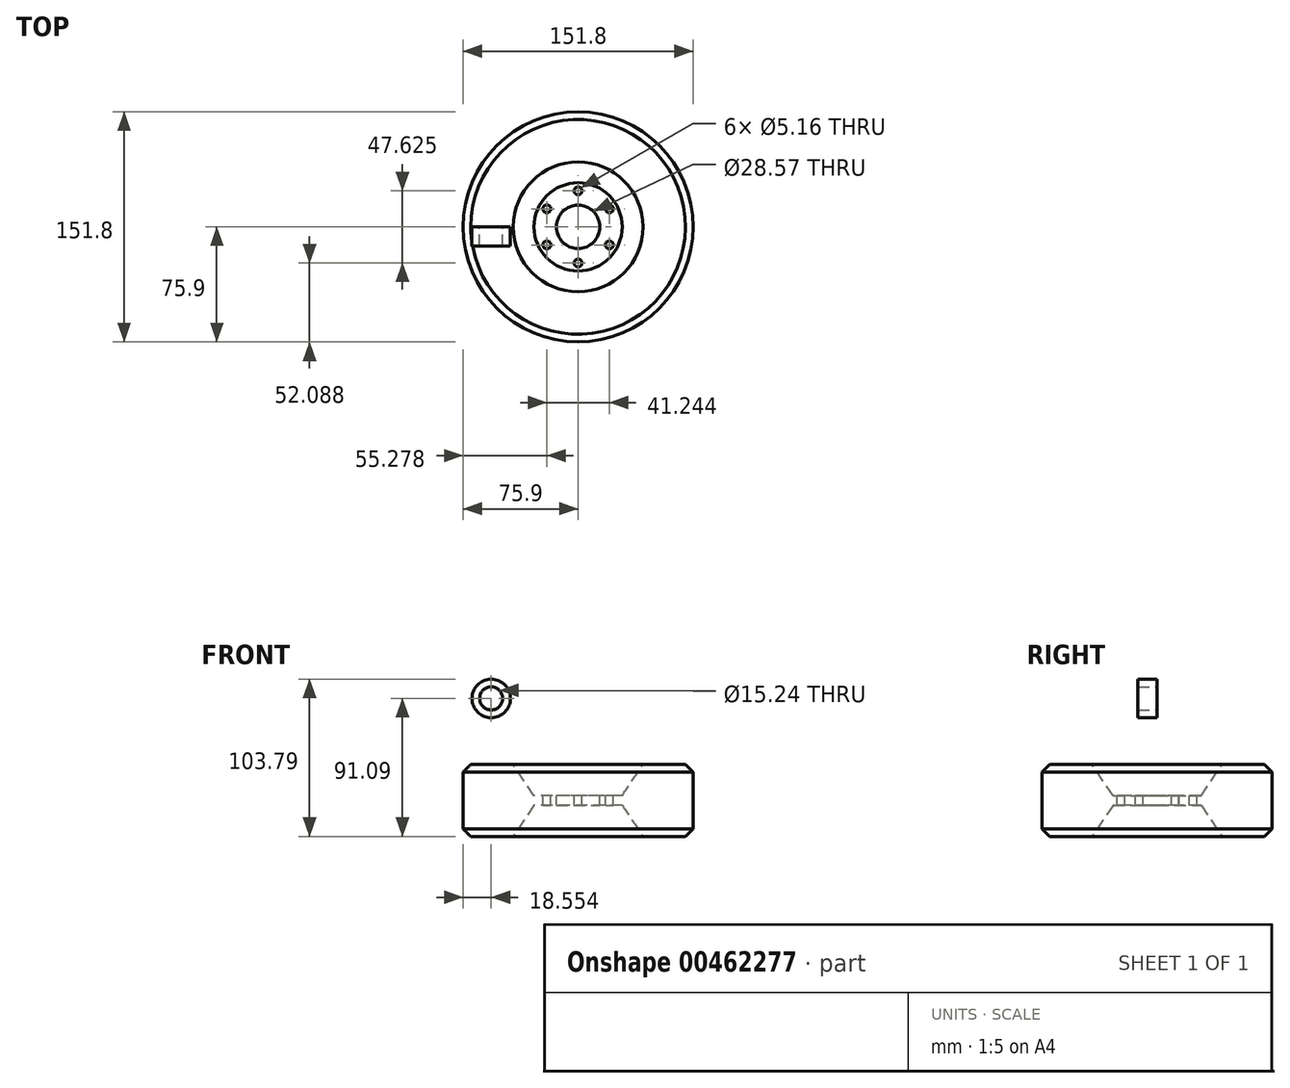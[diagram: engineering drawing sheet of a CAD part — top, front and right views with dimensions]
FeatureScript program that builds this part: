
annotation { "Feature Type Name" : "Feature", "Feature Type Description" : "" }
export const myFeature = defineFeature(function(context is Context, id is Id, definition is map)
    precondition{}
    {
        {
            var Q0;
            Q0=qCreatedBy(makeId("Front.planeOp"),FACE);
            var sketch = newSketch(context, id + "F0", { "sketchPlane" : qUnion([Q0])});
            skLineSegment(sketch, "E0.bottom", {"start": v(-75.9, 23.79) * mm, "end": v(-42.86, 23.79) * mm});
            skLineSegment(sketch, "E0.top", {"start": v(-75.9, -23.79) * mm, "end": v(-42.86, -23.79) * mm});
            skLineSegment(sketch, "E0.left", {"start": v(-75.9, 23.79) * mm, "end": v(-75.9, -23.79) * mm});
            skLineSegment(sketch, "E0.right", {"start": v(75.9, 23.79) * mm, "end": v(75.9, -23.79) * mm, "construction": true});
            skPoint(sketch, "E0.middle", {"position": v(0, 0) * mm});
            skLineSegment(sketch, "E1.bottom", {"start": v(-42.86, 23.79) * mm, "end": v(42.86, 23.79) * mm, "construction": true});
            skLineSegment(sketch, "E1.top", {"start": v(-42.86, -23.79) * mm, "end": v(42.86, -23.79) * mm, "construction": true});
            skLineSegment(sketch, "E1.left", {"start": v(-42.86, 23.79) * mm, "end": v(-42.86, -23.79) * mm, "construction": true});
            skLineSegment(sketch, "E1.right", {"start": v(42.86, 23.79) * mm, "end": v(42.86, -23.79) * mm, "construction": true});
            skLineSegment(sketch, "E2.bottom", {"start": v(-29.1, 3.18) * mm, "end": v(0, 3.18) * mm});
            skLineSegment(sketch, "E2.top", {"start": v(-29.1, -3.18) * mm, "end": v(0, -3.18) * mm});
            skLineSegment(sketch, "E2.left", {"start": v(-29.1, 3.18) * mm, "end": v(-29.1, -3.17) * mm, "construction": true});
            skLineSegment(sketch, "E2.right", {"start": v(29.1, 3.18) * mm, "end": v(29.1, -3.18) * mm, "construction": true});
            skLineSegment(sketch, "E3", {"start": v(-42.86, 23.79) * mm, "end": v(75.9, 23.79) * mm, "construction": true});
            skLineSegment(sketch, "E4", {"start": v(-42.86, -23.79) * mm, "end": v(75.9, -23.79) * mm, "construction": true});
            skLineSegment(sketch, "E5", {"start": v(-42.86, 23.79) * mm, "end": v(-29.1, 3.18) * mm});
            skLineSegment(sketch, "E6", {"start": v(-42.86, -23.79) * mm, "end": v(-29.1, -3.18) * mm});
            skLineSegment(sketch, "E7", {"start": v(0, 23.79) * mm, "end": v(0, -23.79) * mm});
            skLineSegment(sketch, "E8", {"start": v(0, 3.18) * mm, "end": v(29.1, 3.18) * mm, "construction": true});
            skLineSegment(sketch, "E9", {"start": v(0, -3.18) * mm, "end": v(29.1, -3.18) * mm, "construction": true});
            skSolve(sketch);
        }
        {
            var Q0;
            Q0=makeQuery(id+"F0.imprint","IMPRINT",FACE,{"disambiguationData":[TD([[makeQuery(id+"F0.imprint","IMPRINT",EDGE,{"derivedFrom":sQuery(id+"F0.wireOp",EDGE,"E0.bottom")}),-1.0]])]});
            var Q1;
            Q1=sQuery(id+"F0.wireOp",EDGE,"E7");
            revolve(context, id + "F1", {"entities" : qUnion([Q0]), "axis" : qUnion([Q1]), "revolveType" : RevolveType.FULL});
        }
        {
            var Q0;
            Q0=makeQuery(id+"F1.opRevolve","SWEPT_FACE",FACE,{"disambiguationData":[OSD([sQuery(id+"F0.wireOp",EDGE,"E2.bottom")])]});
            var sketch = newSketch(context, id + "F2", { "sketchPlane" : qUnion([Q0])});
            skCircle(sketch, "E10", {"center": v(0, 0) * mm, "radius": 23.81 * mm, "construction": true});
            skCircle(sketch, "E11", {"center": v(0, 0) * mm, "radius": 14.29 * mm});
            skCircle(sketch, "E12", {"center": v(0, 23.81) * mm, "radius": 2.58 * mm});
            skCircle(sketch, "E13.1.1", {"center": v(-20.62, 11.9) * mm, "radius": 2.58 * mm});
            skCircle(sketch, "E13.2.1", {"center": v(-20.62, -11.9) * mm, "radius": 2.58 * mm});
            skCircle(sketch, "E14.2.3.0", {"center": v(0, -23.81) * mm, "radius": 2.58 * mm});
            skCircle(sketch, "E14.2.4.0", {"center": v(20.62, -11.9) * mm, "radius": 2.58 * mm});
            skCircle(sketch, "E14.2.5.0", {"center": v(20.62, 11.9) * mm, "radius": 2.58 * mm});
            skLineSegment(sketch, "E15", {"start": v(0, 23.81) * mm, "end": v(0, 0) * mm, "construction": true});
            skSolve(sketch);
        }
        {
            var Q0;
            Q0=makeQuery(id+"F2.imprint","IMPRINT",FACE,{"disambiguationData":[TD([[makeQuery(id+"F2.imprint","IMPRINT",EDGE,{"derivedFrom":sQuery(id+"F2.wireOp",EDGE,"E13.1.1")}),1.0]])]});
            var Q1;
            Q1=makeQuery(id+"F2.imprint","IMPRINT",FACE,{"disambiguationData":[TD([[makeQuery(id+"F2.imprint","IMPRINT",EDGE,{"derivedFrom":sQuery(id+"F2.wireOp",EDGE,"E13.2.1")}),1.0]])]});
            var Q2;
            Q2=makeQuery(id+"F2.imprint","IMPRINT",FACE,{"disambiguationData":[TD([[makeQuery(id+"F2.imprint","IMPRINT",EDGE,{"derivedFrom":sQuery(id+"F2.wireOp",EDGE,"E11")}),1.0]])]});
            var Q3;
            Q3=makeQuery(id+"F2.imprint","IMPRINT",FACE,{"disambiguationData":[TD([[makeQuery(id+"F2.imprint","IMPRINT",EDGE,{"derivedFrom":sQuery(id+"F2.wireOp",EDGE,"E14.2.5.0")}),1.0]])]});
            var Q4;
            Q4=makeQuery(id+"F2.imprint","IMPRINT",FACE,{"disambiguationData":[TD([[makeQuery(id+"F2.imprint","IMPRINT",EDGE,{"derivedFrom":sQuery(id+"F2.wireOp",EDGE,"E12")}),1.0]])]});
            var Q5;
            Q5=makeQuery(id+"F2.imprint","IMPRINT",FACE,{"disambiguationData":[TD([[makeQuery(id+"F2.imprint","IMPRINT",EDGE,{"derivedFrom":sQuery(id+"F2.wireOp",EDGE,"E14.2.3.0")}),1.0]])]});
            var Q6;
            Q6=makeQuery(id+"F2.imprint","IMPRINT",FACE,{"disambiguationData":[TD([[makeQuery(id+"F2.imprint","IMPRINT",EDGE,{"derivedFrom":sQuery(id+"F2.wireOp",EDGE,"E14.2.4.0")}),1.0]])]});
            extrude(context, id + "F3", {"entities" : qUnion([Q0, Q1, Q2, Q3, Q4, Q5, Q6]), "operationType" : NewBodyOperationType.REMOVE, "endBound" : BoundingType.THROUGH_ALL, "oppositeDirection" : true, "depth" : 25.4 * mm});
        }
        {
            var Q0;
            Q0=makeQuery(id+"F1.opRevolve","SWEPT_EDGE",EDGE,{"disambiguationData":[OSD([sQuery(id+"F0.wireOp",EDGE,"E0.bottom"),sQuery(id+"F0.wireOp",EDGE,"E0.left")])]});
            var Q1;
            Q1=makeQuery(id+"F1.opRevolve","SWEPT_EDGE",EDGE,{"disambiguationData":[OSD([sQuery(id+"F0.wireOp",EDGE,"E0.top"),sQuery(id+"F0.wireOp",EDGE,"E0.left")])]});
            chamfer(context, id + "F4", {"entities" : qUnion([Q0, Q1]), "width" : 5.08 * mm, "tangentPropagation" : true});
        }
        {
            var Q0;
            Q0=qCreatedBy(makeId("Front.planeOp"),FACE);
            var sketch = newSketch(context, id + "F5", { "sketchPlane" : qUnion([Q0])});
            skCircle(sketch, "E16", {"center": v(-57.35, 67.3) * mm, "radius": 12.7 * mm});
            skCircle(sketch, "E17", {"center": v(-57.35, 67.3) * mm, "radius": 7.62 * mm});
            skSolve(sketch);
        }
        {
            var Q0;
            Q0=makeQuery(id+"F5.imprint","IMPRINT",FACE,{"disambiguationData":[TD([[makeQuery(id+"F5.imprint","IMPRINT",EDGE,{"derivedFrom":sQuery(id+"F5.wireOp",EDGE,"E16")}),1.0]])]});
            extrude(context, id + "F6", {"entities" : qUnion([Q0]), "depth" : 12.7 * mm});
        }
    });
